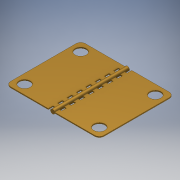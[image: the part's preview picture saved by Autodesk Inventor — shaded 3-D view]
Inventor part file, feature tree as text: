
AUTODESK INVENTOR PART (.ipt)
format: ipt  version: 2018.3 (Build 223284000, 284)  size: 223,232 bytes
history: native  units: mm
features: sketch x6, extrude x4, hole x2, fillet x1
ambient origin geometry x8: Origin, YZ Plane, XZ Plane, XY Plane, X Axis, Y Axis, Z Axis, Center Point
bodies: Solid1 (feature_tree)
feature tree (13):
  extrude  "Extrusion1"  Depth=8.0mm
  extrude  "Extrusion2"  Depth=0.1mm
  hole  "Hole1"  [1 undecoded]
  hole  "Hole2"  [1 undecoded]
  extrude  "Extrusion3"  Depth=0.5mm
  extrude  "Extrusion4"  Depth=0.5mm
  fillet  "Fillet1"  Radius=0.5mm
  sketch  "Sketch1"  dims[d0=10.0mm d1=8.0mm]
  sketch  "Sketch2"  dims[d2=0.1mm d3=0.0mm d4=0.45mm]
  sketch  "Sketch3"  dims[d5=8.0mm d6=0.0mm]
  sketch  "Sketch4"  dims[d7=1.2mm d8=6.0mm d9=4.0mm d10=2.0mm d11=90.0deg d12=8.0mm d13=20.594885mm]
  sketch  "Sketch5"  dims[d14=1.2mm d15=6.0mm d16=4.0mm d17=2.0mm d18=90.0deg d19=8.0mm d20=20.594885mm d21=0.25mm]
  sketch  "Sketch6"  dims[d22=0.5mm d23=0.5mm d24=0.5mm d25=0.5mm d26=0.5mm d27=0.5mm d28=0.5mm d29=0.5mm d30=8.0mm d31=0.0mm d32=0.25mm d33=0.5mm d36=0.5mm d37=0.5mm d38=0.5mm d39=0.5mm d40=0.5mm d41=0.5mm d42=8.0mm d43=0.0mm d44=0.5mm]
note: 2 required parameter values undecoded (feature->parameter linkage not recoverable at this tier; creation-order binding heuristic only, values carry confidence <= 0.55)
